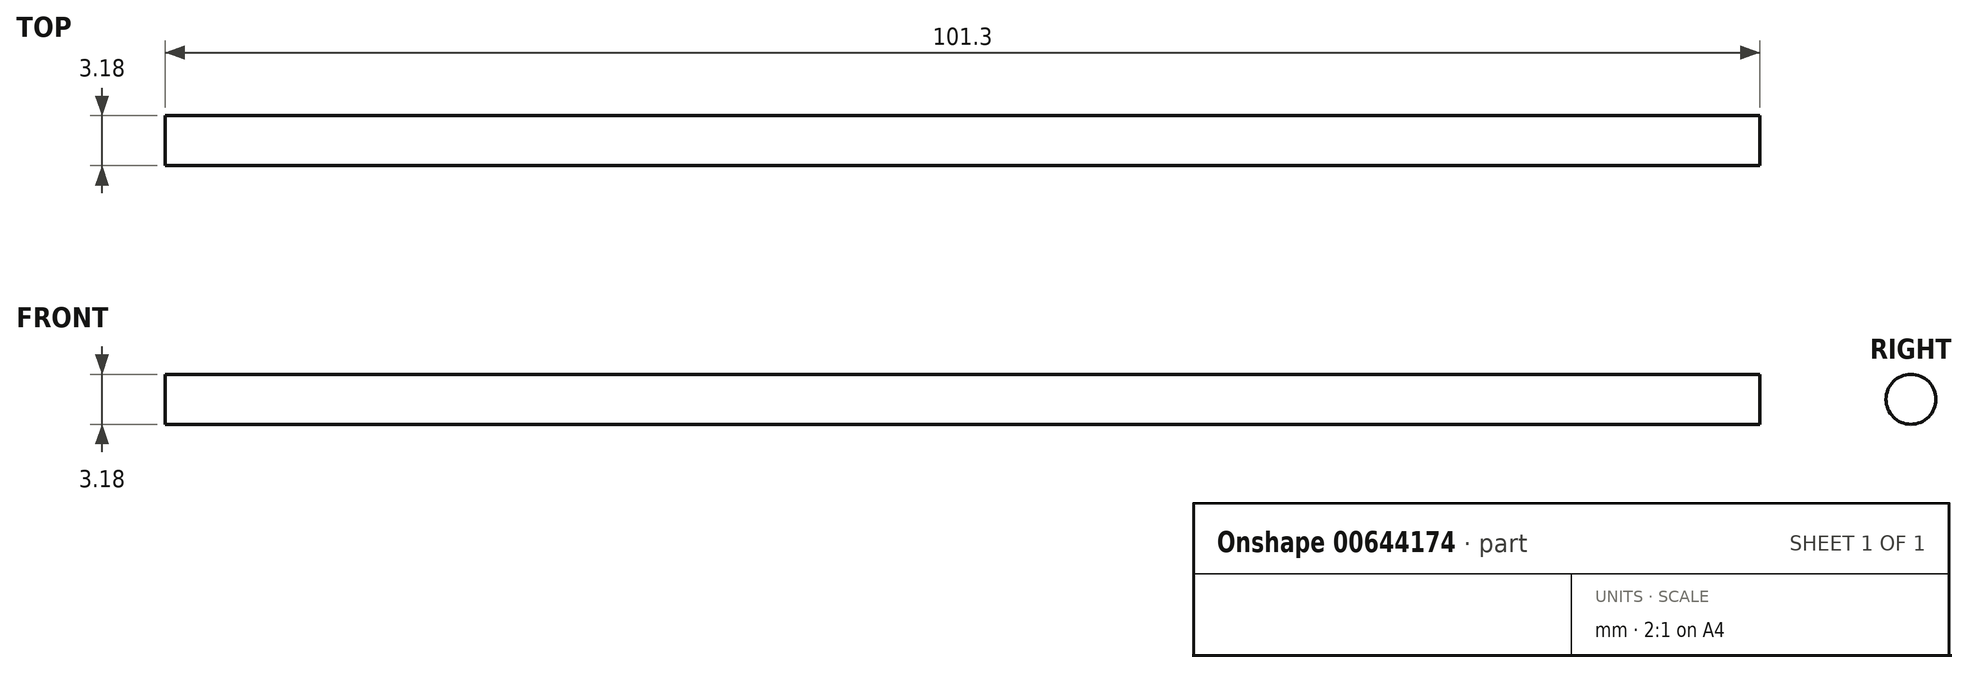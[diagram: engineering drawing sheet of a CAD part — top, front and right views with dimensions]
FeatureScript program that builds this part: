
annotation { "Feature Type Name" : "Feature", "Feature Type Description" : "" }
export const myFeature = defineFeature(function(context is Context, id is Id, definition is map)
    precondition{}
    {
        {
            var Q0;
            Q0=qCreatedBy(makeId("Right.planeOp"),FACE);
            var sketch = newSketch(context, id + "F0", { "sketchPlane" : qUnion([Q0])});
            skCircle(sketch, "E0", {"center": v(0, 0) * mm, "radius": 1.59 * mm});
            skSolve(sketch);
        }
        {
            var Q0;
            Q0 = qSketchRegion(id + "F0", true);
            extrude(context, id + "F1", {"entities" : qUnion([Q0]), "depth" : 50.65 * mm, "offsetDistance" : 25.4 * mm, "hasSecondDirection" : true, "secondDirectionOppositeDirection" : true, "secondDirectionDepth" : 50.65 * mm});
        }
    });
